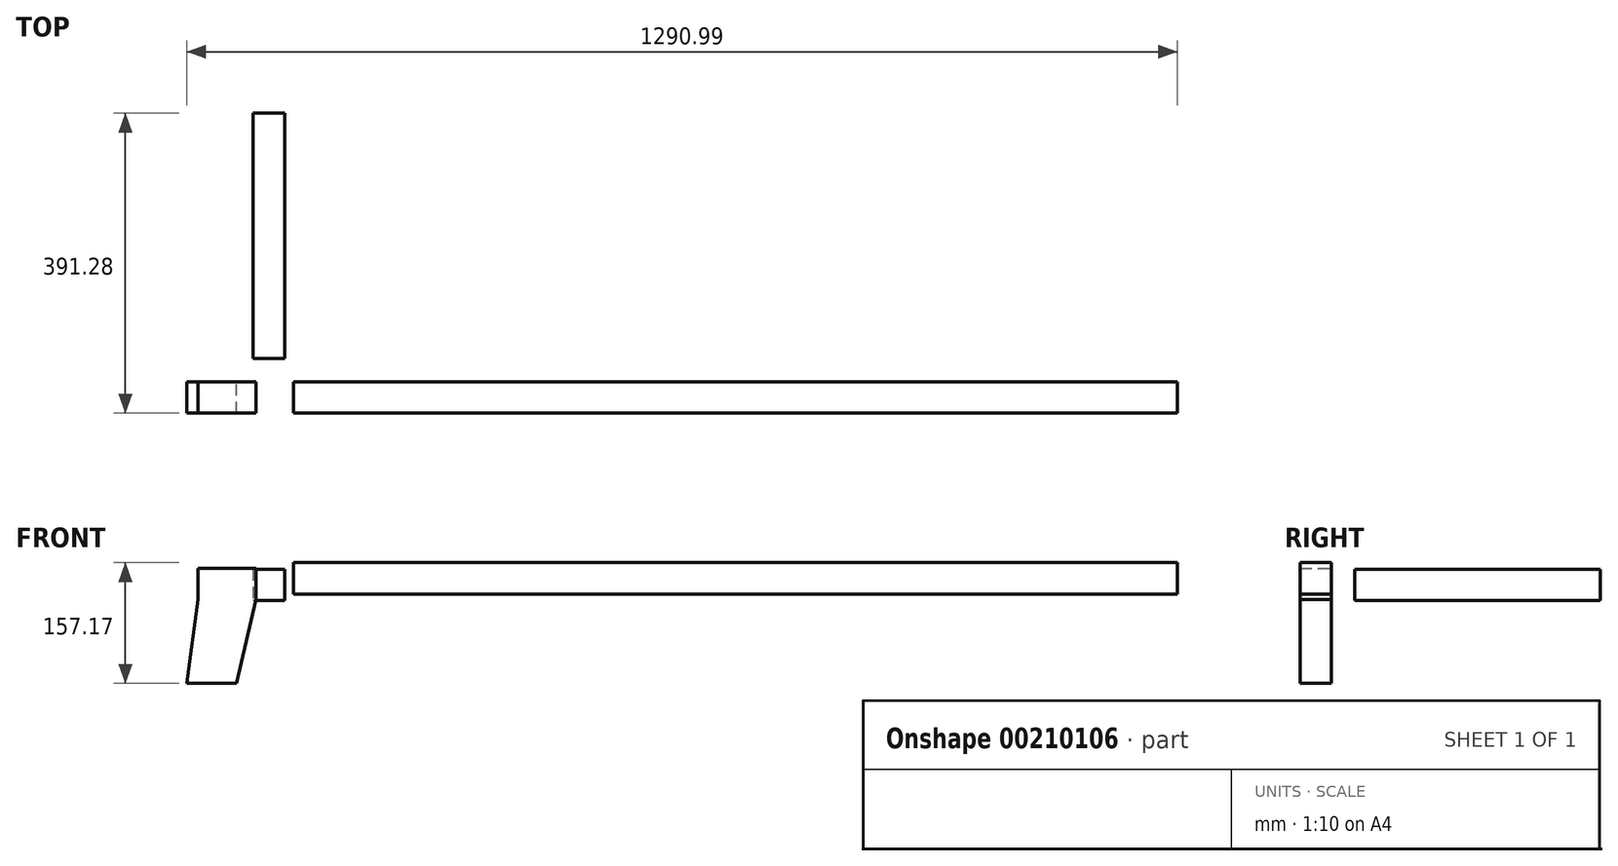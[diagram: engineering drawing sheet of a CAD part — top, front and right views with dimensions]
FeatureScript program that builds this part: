
annotation { "Feature Type Name" : "Feature", "Feature Type Description" : "" }
export const myFeature = defineFeature(function(context is Context, id is Id, definition is map)
    precondition{}
    {
        {
            var Q0;
            Q0=qCreatedBy(makeId("Front.planeOp"),FACE);
            var sketch = newSketch(context, id + "F0", { "sketchPlane" : qUnion([Q0])});
            skLineSegment(sketch, "E0", {"start": v(-71.59, 78.64) * mm, "end": v(-71.59, 37.64) * mm});
            skLineSegment(sketch, "E1", {"start": v(-71.59, 37.64) * mm, "end": v(-86.59, -71.36) * mm});
            skLineSegment(sketch, "E2", {"start": v(-86.59, -71.36) * mm, "end": v(-21.65, -71.36) * mm});
            skLineSegment(sketch, "E3", {"start": v(-21.65, -71.36) * mm, "end": v(3.41, 37.64) * mm});
            skLineSegment(sketch, "E4", {"start": v(3.41, 37.64) * mm, "end": v(3.41, 78.64) * mm});
            skLineSegment(sketch, "E5", {"start": v(3.41, 78.64) * mm, "end": v(-71.59, 78.64) * mm});
            skSolve(sketch);
        }
        {
            var Q0;
            Q0 = qSketchRegion(id + "F0", true);
            extrude(context, id + "F1", {"entities" : qUnion([Q0]), "depth" : 41 * mm});
        }
        {
            var Q0;
            Q0=qCreatedBy(makeId("Front.planeOp"),FACE);
            var sketch = newSketch(context, id + "F2", { "sketchPlane" : qUnion([Q0])});
            skLineSegment(sketch, "E6", {"start": v(52.4, 85.81) * mm, "end": v(52.4, 44.81) * mm});
            skLineSegment(sketch, "E7", {"start": v(52.4, 44.81) * mm, "end": v(1204.4, 44.81) * mm});
            skLineSegment(sketch, "E8", {"start": v(1204.4, 44.81) * mm, "end": v(1204.4, 85.81) * mm});
            skLineSegment(sketch, "E9", {"start": v(1204.4, 85.81) * mm, "end": v(52.4, 85.81) * mm});
            skSolve(sketch);
        }
        {
            var Q0;
            Q0 = qSketchRegion(id + "F2", true);
            extrude(context, id + "F3", {"entities" : qUnion([Q0]), "depth" : 41 * mm});
        }
        {
            var Q0;
            Q0=qCreatedBy(makeId("Right.planeOp"),FACE);
            var sketch = newSketch(context, id + "F4", { "sketchPlane" : qUnion([Q0])});
            skLineSegment(sketch, "E10", {"start": v(30.28, 77.41) * mm, "end": v(30.28, 36.41) * mm});
            skLineSegment(sketch, "E11", {"start": v(30.28, 36.41) * mm, "end": v(350.28, 36.41) * mm});
            skLineSegment(sketch, "E12", {"start": v(350.28, 36.41) * mm, "end": v(350.28, 77.41) * mm});
            skLineSegment(sketch, "E13", {"start": v(350.28, 77.41) * mm, "end": v(30.28, 77.41) * mm});
            skSolve(sketch);
        }
        {
            var Q0;
            Q0 = qSketchRegion(id + "F4", true);
            extrude(context, id + "F5", {"entities" : qUnion([Q0]), "depth" : 41 * mm});
        }
    });
